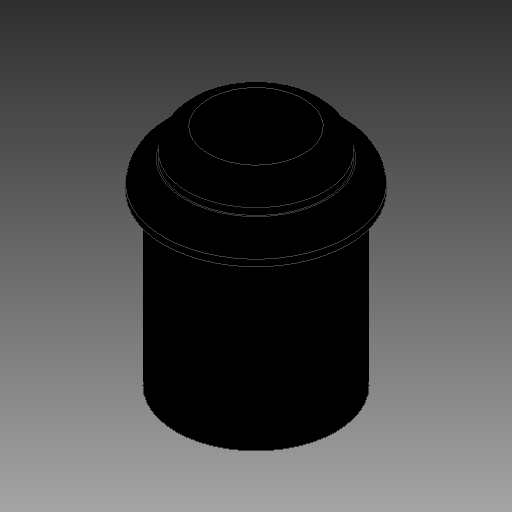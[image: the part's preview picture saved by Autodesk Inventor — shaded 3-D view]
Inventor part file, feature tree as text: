
AUTODESK INVENTOR PART (.ipt)
format: ipt  version: 2017 (Build 210142000, 142)  size: 136,704 bytes
history: native  units: in
note: dims shown in document units (in); Inventor stores cm internally (conversion verified against a paired STEP export)
features: extrude x3, sketch x3, fillet x2
ambient origin geometry x8: Origin, YZ Plane, XZ Plane, XY Plane, X Axis, Y Axis, Z Axis, Center Point
bodies: Solid1 (feature_tree)
feature tree (8):
  extrude  "Extrusion1"  Depth=0.1634in TaperAngle=0.0deg
  extrude  "Extrusion2"  Depth=0.1634in TaperAngle=0.0deg
  fillet  "Fillet1"  Radius=0.125in
  fillet  "Fillet2"  Radius=0.125in
  extrude  "Extrusion3"  Depth=0.9724in TaperAngle=0.0deg
  sketch  "Sketch1"  dims[d0=1.0669in d1=0.1634in d2=0.0in]
  sketch  "Sketch2"  dims[d3=0.8002in d4=0.1634in d5=0.0in d6=0.125in d7=0.125in]
  sketch  "Sketch3"  dims[d8=0.9252in d9=0.9724in d10=0.0in]
